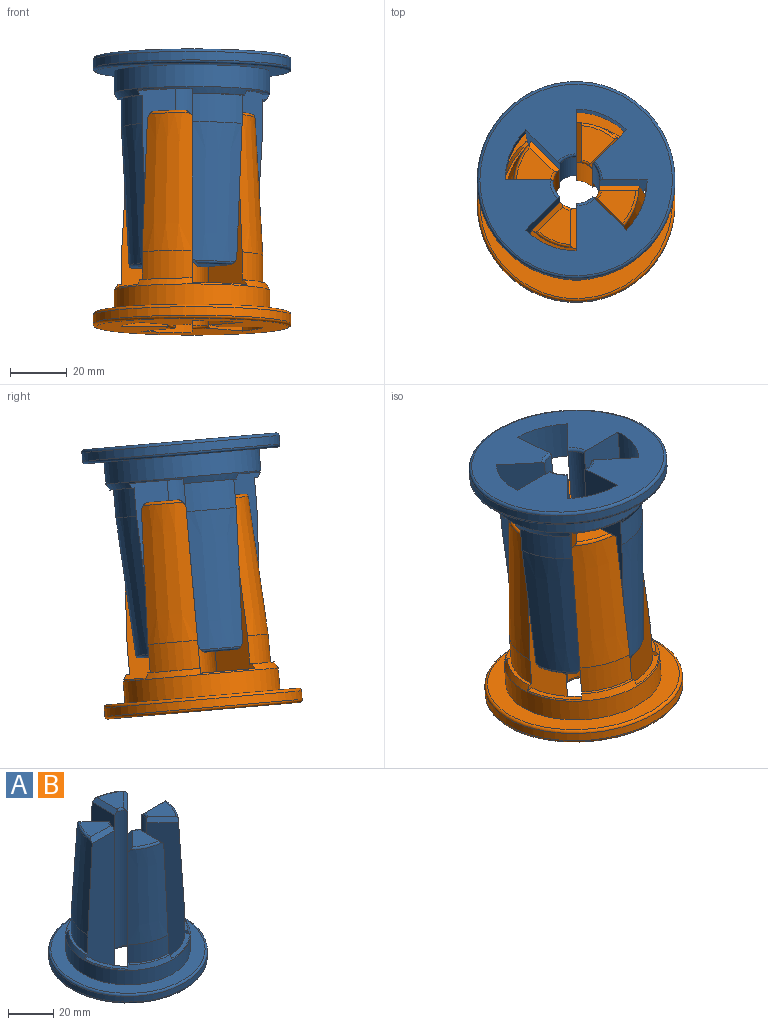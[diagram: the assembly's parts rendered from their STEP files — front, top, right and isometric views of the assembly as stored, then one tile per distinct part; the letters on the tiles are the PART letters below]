
ASSEMBLY  parts=2 mates=2
PART A: 63 faces, bbox 75.8x75.8x75 mm
  f0: cylinder r=8.25mm len=73mm, axis (0,0,-1), area 472mm2, adj f16,f35,f41,f50,f55,f56
  f1: cylinder r=8.25mm len=73mm, axis (0,0,-1), area 472mm2, adj f5,f14,f45,f47,f59,f60
  f2: cylinder r=8.25mm len=73mm, axis (0,0,-1), area 472mm2, adj f3,f13,f48,f49,f61,f62
  f3: torus R=9.25mm, axis (0,0,-1), area 10.6mm2, adj f2,f6,f48,f49
  f4: torus R=9.25mm, axis (0,0,-1), area 10.6mm2, adj f6,f17,f42,f44
  f5: torus R=9.25mm, axis (0,0,-1), area 10.6mm2, adj f1,f6,f45,f47
  f6: plane 68x68mm, normal (0,0,-1), area 2505.5mm2, adj f3,f4,f5,f35,f36,f41,f42,f44
  f7: plane 19.23x9.43mm, normal (0,0,1), area 42.5mm2, adj f18,f41,f42,f51
  f8: plane 19.23x9.43mm, normal (0,0,1), area 42.5mm2, adj f18,f49,f50,f54
  f9: plane 13.35x11.54mm, normal (0,0,1), area 95.5mm2, adj f13,f31,f61,f62
  f10: plane 13.35x11.54mm, normal (0,0,1), area 95.5mm2, adj f14,f32,f59,f60
  f11: plane 13.35x11.54mm, normal (0,0,1), area 95.5mm2, adj f15,f33,f57,f58
  f12: plane 13.35x11.54mm, normal (0,0,1), area 95.5mm2, adj f16,f34,f55,f56
  f13: torus R=9.25mm, axis (0,0,-1), area 5.5mm2, adj f2,f9,f61,f62
  f14: torus R=9.25mm, axis (0,0,-1), area 5.5mm2, adj f1,f10,f59,f60
  f15: torus R=9.25mm, axis (0,0,-1), area 5.5mm2, adj f11,f17,f57,f58
  f16: torus R=9.25mm, axis (0,0,-1), area 5.5mm2, adj f0,f12,f55,f56
  f17: cylinder r=8.25mm len=73mm, axis (0,0,-1), area 472mm2, adj f4,f15,f42,f44,f57,f58
  f18: cone r=26.25mm half-angle=29.2deg, axis (0,0,-1), area 269.9mm2, adj f7,f8,f19,f20,f21,f22,f40,f41
  f19: plane 18.56x8.57mm, normal (0,0,1), area 25.2mm2, adj f18,f23,f48,f49
  f20: plane 18.56x8.57mm, normal (0,0,1), area 25.2mm2, adj f18,f24,f45,f47
  f21: plane 18.56x8.57mm, normal (0,0,1), area 25.2mm2, adj f18,f25,f42,f44
  f22: plane 18.56x8.57mm, normal (0,0,1), area 25.2mm2, adj f18,f26,f41,f50
  f23: cylinder r=25mm len=17.68mm, axis (0,0,-1), area 196.3mm2, adj f19,f27,f48,f49
  f24: cylinder r=25mm len=17.68mm, axis (0,0,-1), area 196.3mm2, adj f20,f28,f45,f47
  f25: cylinder r=25mm len=17.68mm, axis (0,0,-1), area 196.3mm2, adj f21,f29,f42,f44
  f26: cylinder r=25mm len=17.68mm, axis (0,0,-1), area 196.3mm2, adj f22,f30,f41,f50
  f27: cone r=25mm half-angle=3.2deg, axis (0,0,-1), area 910.4mm2, adj f23,f31,f48,f49,f61,f62
  f28: cone r=25mm half-angle=3.2deg, axis (0,0,-1), area 910.4mm2, adj f24,f32,f45,f47,f59,f60
  f29: cone r=25mm half-angle=3.2deg, axis (0,0,-1), area 910.4mm2, adj f25,f33,f42,f44,f57,f58
  f30: cone r=25mm half-angle=3.2deg, axis (0,0,-1), area 910.4mm2, adj f26,f34,f41,f50,f55,f56
  f31: torus R=21.24mm, axis (0,0,-1), area 21mm2, adj f9,f27,f61,f62
  f32: torus R=21.24mm, axis (0,0,-1), area 21mm2, adj f10,f28,f59,f60
  f33: torus R=21.24mm, axis (0,0,-1), area 21mm2, adj f11,f29,f57,f58
  f34: torus R=21.24mm, axis (0,0,-1), area 21mm2, adj f12,f30,f55,f56
  f35: torus R=9.25mm, axis (0,0,-1), area 10.6mm2, adj f0,f6,f41,f50
  f36: torus R=34mm, axis (0,0,-1), area 341.8mm2, adj f6,f37
  f37: cylinder r=35mm len=70mm, axis (0,0,-1), area 659.7mm2, adj f36,f38
  f38: torus R=34mm, axis (0,0,-1), area 341.8mm2, adj f37,f39
  f39: plane 68x68mm, normal (0,0,1), area 1255.9mm2, adj f38,f40
  f40: cylinder r=27.5mm len=55mm, axis (0,0,-1), area 1340.7mm2, adj f18,f39
  f41: plane 73x13.4mm, normal (-0.71,0.71,0), area 1162.4mm2, adj f0,f6,f7,f18,f22,f26,f30,f35
  f42: plane 73x18.95mm, normal (0,-1,0), area 1162.4mm2, adj f4,f6,f7,f17,f18,f21,f25,f29
  f43: plane 19.23x9.43mm, normal (0,0,1), area 42.5mm2, adj f18,f44,f45,f53
  f44: plane 73x13.4mm, normal (0.71,0.71,0), area 1162.4mm2, adj f4,f6,f17,f18,f21,f25,f29,f43
  f45: plane 73x18.95mm, normal (-1,0,0), area 1162.4mm2, adj f1,f5,f6,f18,f20,f24,f28,f43
  f46: plane 19.23x9.43mm, normal (0,0,1), area 42.5mm2, adj f18,f47,f48,f52
  f47: plane 73x13.4mm, normal (0.71,-0.71,0), area 1162.4mm2, adj f1,f5,f6,f18,f20,f24,f28,f46
  f48: plane 73x18.95mm, normal (0,1,0), area 1162.4mm2, adj f2,f3,f6,f18,f19,f23,f27,f46
  f49: plane 73x13.4mm, normal (-0.71,-0.71,0), area 1162.4mm2, adj f2,f3,f6,f8,f18,f19,f23,f27
  f50: plane 73x18.95mm, normal (1,0,0), area 1162.4mm2, adj f0,f6,f8,f18,f22,f26,f30,f35
  f51: cylinder r=25.13mm len=17.77mm, axis (0,0,1), area 262.5mm2, adj f6,f7,f41,f42
  f52: cylinder r=25.13mm len=17.77mm, axis (0,0,1), area 262.5mm2, adj f6,f46,f47,f48
  f53: cylinder r=25.13mm len=17.77mm, axis (0,0,1), area 262.5mm2, adj f6,f43,f44,f45
  f54: cylinder r=25.13mm len=17.77mm, axis (0,0,1), area 262.5mm2, adj f6,f8,f49,f50
  f55: plane 14.12x2mm, normal (0.71,0,0.71), area 39.2mm2, adj f0,f12,f16,f30,f34,f50
  f56: plane 11.06x10.85mm, normal (-0.5,0.5,0.71), area 39.2mm2, adj f0,f12,f16,f30,f34,f41
  f57: plane 14.12x2mm, normal (0,-0.71,0.71), area 39.2mm2, adj f11,f15,f17,f29,f33,f42
  f58: plane 11.06x10.85mm, normal (0.5,0.5,0.71), area 39.2mm2, adj f11,f15,f17,f29,f33,f44
  f59: plane 14.12x2mm, normal (-0.71,0,0.71), area 39.2mm2, adj f1,f10,f14,f28,f32,f45
  f60: plane 11.06x10.85mm, normal (0.5,-0.5,0.71), area 39.2mm2, adj f1,f10,f14,f28,f32,f47
  f61: plane 14.12x2mm, normal (0,0.71,0.71), area 39.2mm2, adj f2,f9,f13,f27,f31,f48
  f62: plane 11.06x10.85mm, normal (-0.5,-0.5,0.71), area 39.2mm2, adj f2,f9,f13,f27,f31,f49
PART B: same geometry as A
PLACE A rot(axis=(1,0,0),175deg) t=(-204.59,-75.86,66.15)mm fixed
PLACE B rot(axis=(-1,0,0),5deg) t=(-204.59,-84.18,-29.06)mm
MATE cylindrical A.f0 <-> B.f0  axis (0,0.09,1) through (-204.59,-75.94,65.15)mm
MATE planar B.f48 <-> A.f48  axis (0,1,-0.09) through (-180.94,-79.91,19.75)mm
